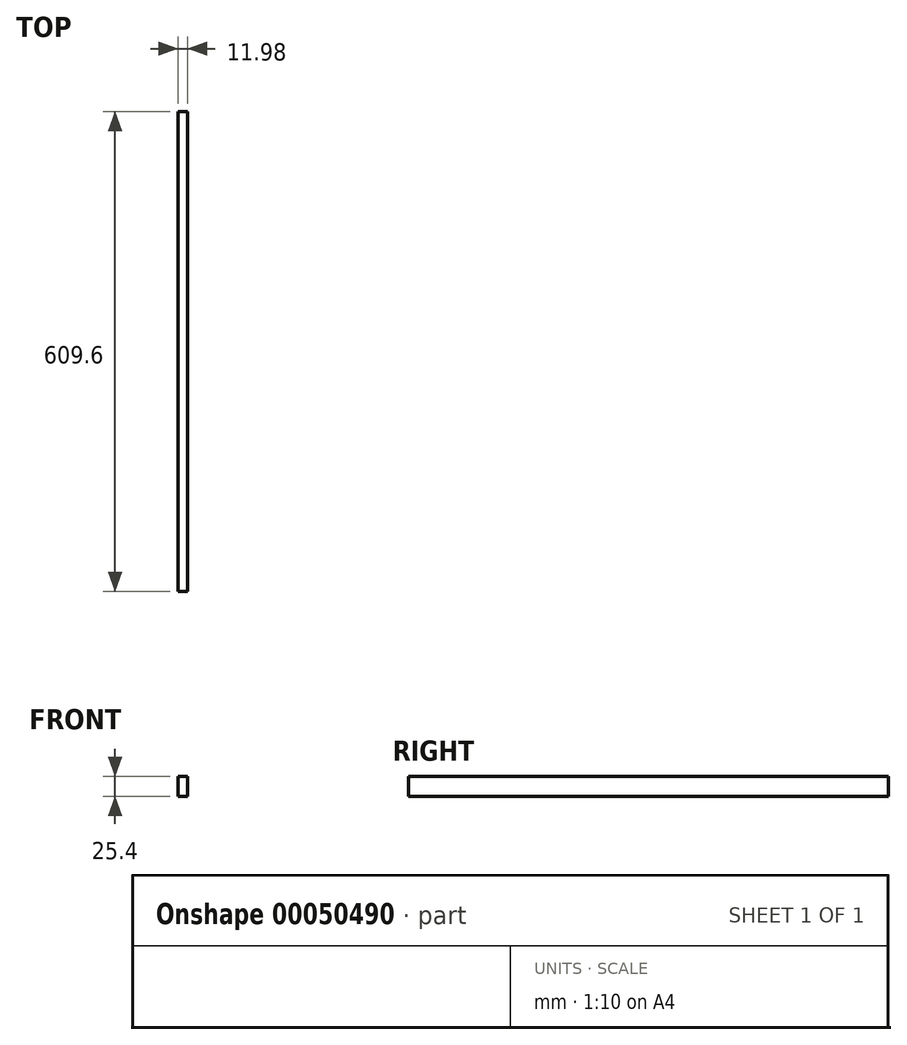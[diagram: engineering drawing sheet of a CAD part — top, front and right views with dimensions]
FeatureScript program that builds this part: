
annotation { "Feature Type Name" : "Feature", "Feature Type Description" : "" }
export const myFeature = defineFeature(function(context is Context, id is Id, definition is map)
    precondition{}
    {
        {
            var Q0;
            Q0=qCreatedBy(makeId("Right.planeOp"),FACE);
            var sketch = newSketch(context, id + "F0", { "sketchPlane" : qUnion([Q0])});
            skLineSegment(sketch, "E0.rect.bottom", {"start": v(304.8, -12.7) * mm, "end": v(-304.8, -12.7) * mm});
            skLineSegment(sketch, "E0.rect.top", {"start": v(304.8, 12.7) * mm, "end": v(-304.8, 12.7) * mm});
            skLineSegment(sketch, "E0.rect.left", {"start": v(304.8, -12.7) * mm, "end": v(304.8, 12.7) * mm});
            skLineSegment(sketch, "E0.rect.right", {"start": v(-304.8, -12.7) * mm, "end": v(-304.8, 12.7) * mm});
            skPoint(sketch, "E0.rect.middle", {"position": v(0, 0) * mm});
            skSolve(sketch);
        }
        {
            var Q0;
            Q0=qSketchRegion(id+"F0",true);
            extrude(context, id + "F1", {"entities" : qUnion([Q0]), "endBound" : BoundingType.SYMMETRIC, "depth" : 12 * mm});
        }
    });
